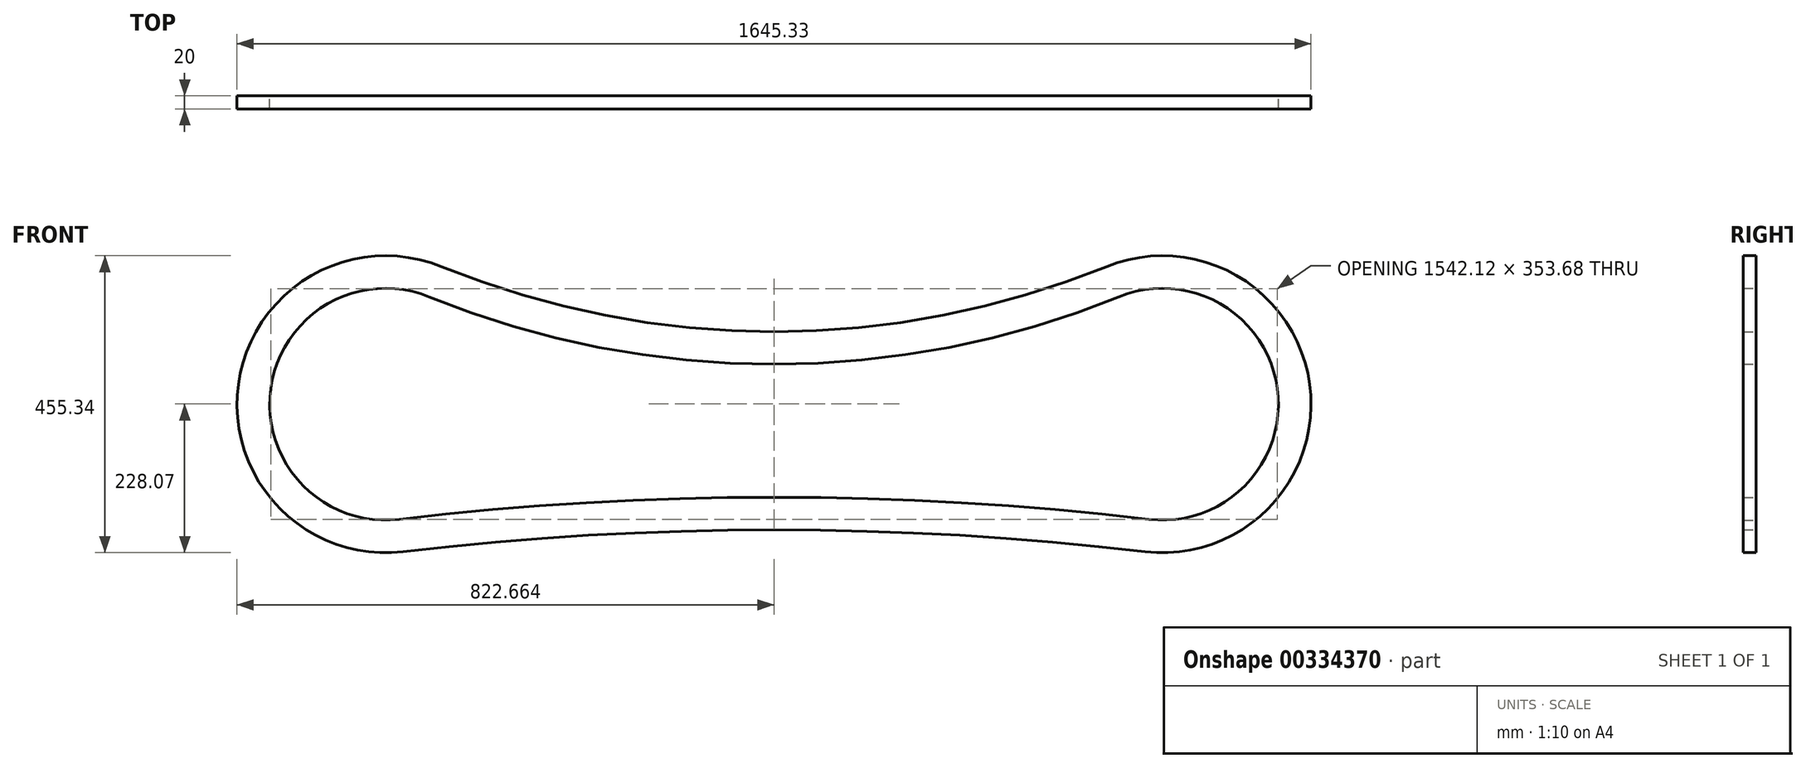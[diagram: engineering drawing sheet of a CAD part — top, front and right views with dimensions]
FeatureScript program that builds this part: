
annotation { "Feature Type Name" : "Feature", "Feature Type Description" : "" }
export const myFeature = defineFeature(function(context is Context, id is Id, definition is map)
    precondition{}
    {
        {
            var Q0;
            Q0=qCreatedBy(makeId("Front.planeOp"),FACE);
            var sketch = newSketch(context, id + "F0", { "sketchPlane" : qUnion([Q0])});
            skArc(sketch, "E0", {"start": v(-508.85, 210.87) * mm, "mid": v(-820.28, 30.54) * mm, "end": v(-568, -226.1) * mm});
            skArc(sketch, "E1", {"start": v(568.65, -226.1) * mm, "mid": v(820.93, 30.54) * mm, "end": v(509.5, 210.87) * mm});
            skLineSegment(sketch, "E2", {"start": v(-594.68, 0) * mm, "end": v(595.32, 0) * mm});
            skArc(sketch, "E3", {"start": v(568.65, -226.1) * mm, "mid": v(0.32, -192.69) * mm, "end": v(-568, -226.1) * mm});
            skPoint(sketch, "E3.centerSnap0", {"position": v(0.32, 0) * mm});
            skArc(sketch, "E4", {"start": v(-508.85, 210.87) * mm, "mid": v(0.32, 111.22) * mm, "end": v(509.5, 210.87) * mm});
            skArc(sketch, "E5.0", {"start": v(-527.7, 164.56) * mm, "mid": v(-770.74, 23.83) * mm, "end": v(-573.86, -176.44) * mm});
            skArc(sketch, "E6.0", {"start": v(-527.7, 164.56) * mm, "mid": v(0.32, 61.22) * mm, "end": v(528.35, 164.56) * mm});
            skArc(sketch, "E7.0", {"start": v(574.5, -176.44) * mm, "mid": v(771.39, 23.83) * mm, "end": v(528.35, 164.56) * mm});
            skArc(sketch, "E8.0", {"start": v(574.5, -176.44) * mm, "mid": v(0.32, -142.69) * mm, "end": v(-573.86, -176.44) * mm});
            skSolve(sketch);
        }
        {
            var Q0;
            Q0=makeQuery(id+"F0.imprint","IMPRINT",FACE,{"disambiguationData":[TD([[makeQuery(id+"F0.imprint","IMPRINT",EDGE,{"derivedFrom":sQuery(id+"F0.wireOp",EDGE,"E0")}),1.0]])]});
            extrude(context, id + "F1", {"entities" : qUnion([Q0]), "depth" : 20 * mm});
        }
    });
